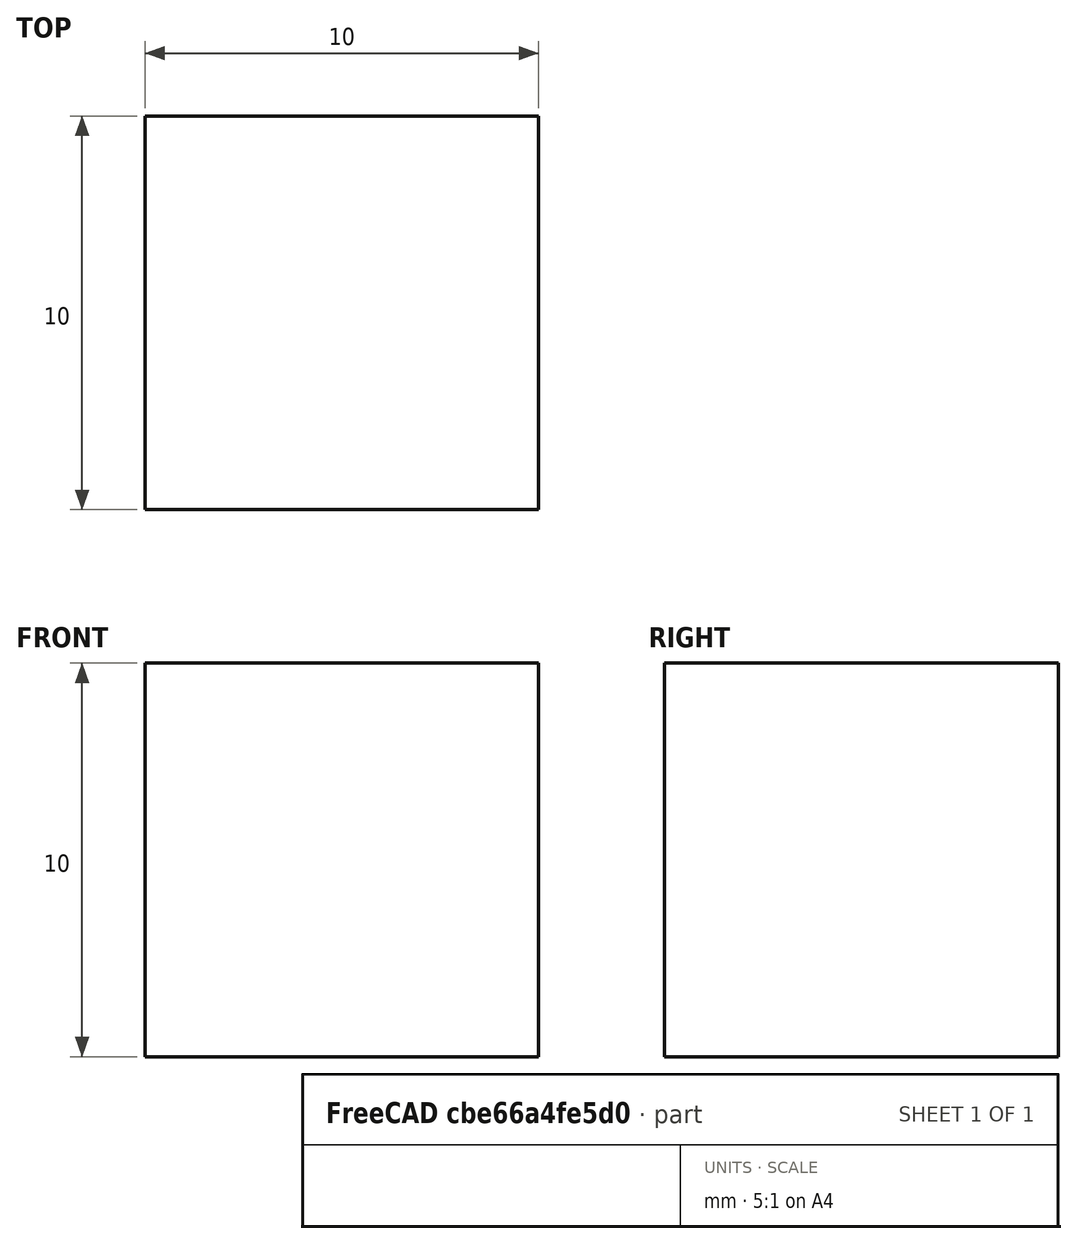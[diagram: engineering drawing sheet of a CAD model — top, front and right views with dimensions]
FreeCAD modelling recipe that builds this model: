
FCSTD DOCUMENT  (FreeCAD 0.20R29177 +426 (Git))
Label: CubexLevel
License: All rights reserved
LicenseURL: http://en.wikipedia.org/wiki/All_rights_reserved
objects: Part::Box×7
note: 7 computed .brp shape members not serialized (recipe doc carries the construction recipe); baked Part::Feature solids carry a one-line shape summary decoded from their .brp

FEATURE [Part::Box] Box  label="Cubo"
  AttacherType = Attacher::AttachEngine3D
  Height = 10
  Length = 10
  Width = 10
FEATURE [Part::Box] Box001  label="Cubo001"
  AttacherType = Attacher::AttachEngine3D
  Height = 10
  Length = 10
  Width = 10
FEATURE [Part::Box] Box002  label="Cubo002"
  AttacherType = Attacher::AttachEngine3D
  Height = 10
  Length = 10
  Width = 10
FEATURE [Part::Box] Box003  label="Cubo003"
  AttacherType = Attacher::AttachEngine3D
  Height = 10
  Length = 10
  Width = 10
FEATURE [Part::Box] Box004  label="Cubo004"
  AttacherType = Attacher::AttachEngine3D
  Height = 10
  Length = 10
  Width = 10
FEATURE [Part::Box] Box005  label="Cubo005"
  AttacherType = Attacher::AttachEngine3D
  Height = 10
  Length = 10
  Width = 10
FEATURE [Part::Box] Box006  label="Cubo006"
  AttacherType = Attacher::AttachEngine3D
  Height = 10
  Length = 10
  Width = 10
